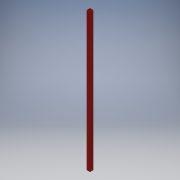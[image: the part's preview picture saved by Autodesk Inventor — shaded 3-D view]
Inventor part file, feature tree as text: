
AUTODESK INVENTOR PART (.ipt)
format: ipt  version: 2017 SP1 (Build 210196100, 196)  size: 107,520 bytes
history: native  units: in
note: dims shown in document units (in); Inventor stores cm internally (conversion verified against a paired STEP export)
features: extrude x2, sketch x2
ambient origin geometry x8: Origin, YZ Plane, XZ Plane, XY Plane, X Axis, Y Axis, Z Axis, Center Point
bodies: Solid1 (feature_tree)
feature tree (4):
  extrude  "Extrusion1"  Depth=0.0625in
  extrude  "Extrusion2"  Depth=40.0in
  sketch  "Sketch1"  dims[d0=1.0in d1=0.0625in]
  sketch  "Sketch2"  dims[d2=40.0in d3=0.0in d4=0.25in d5=0.5in d6=36.0in d7=0.0in]
